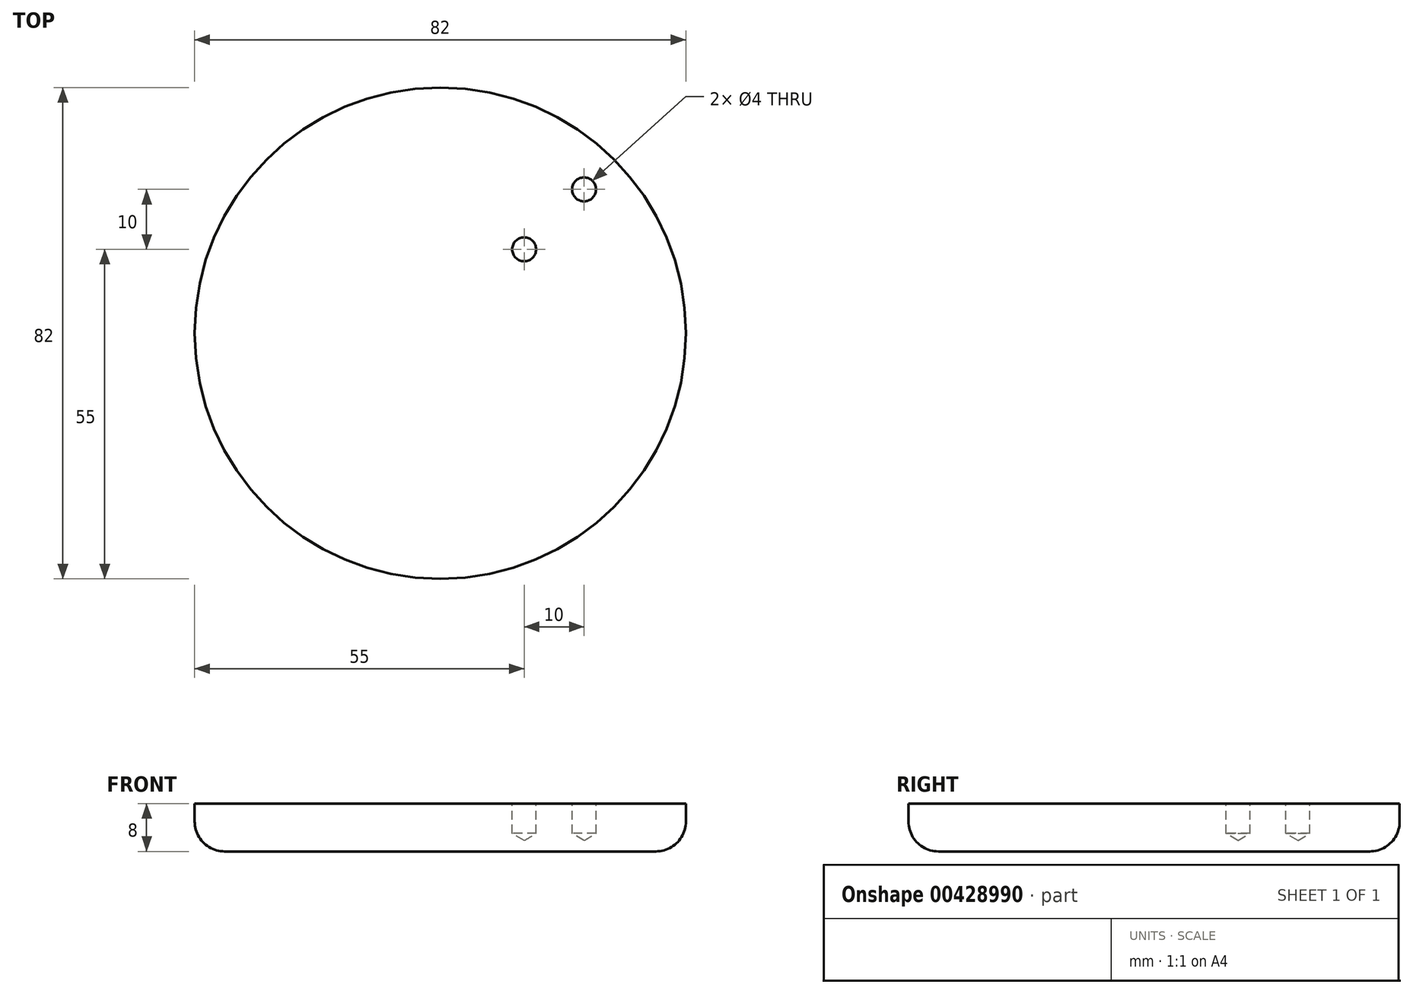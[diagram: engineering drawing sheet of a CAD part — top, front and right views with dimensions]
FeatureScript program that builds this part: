
annotation { "Feature Type Name" : "Feature", "Feature Type Description" : "" }
export const myFeature = defineFeature(function(context is Context, id is Id, definition is map)
    precondition{}
    {
        {
            var Q0;
            Q0=qCreatedBy(makeId("Top.planeOp"),FACE);
            var sketch = newSketch(context, id + "F0", { "sketchPlane" : qUnion([Q0])});
            skCircle(sketch, "E0", {"center": v(0, 0) * mm, "radius": 41 * mm});
            skSolve(sketch);
        }
        {
            var Q0;
            Q0 = qSketchRegion(id + "F0", true);
            extrude(context, id + "F1", {"entities" : qUnion([Q0]), "depth" : 8 * mm});
        }
        {
            var Q0;
            Q0=makeQuery(id+"F1.opExtrude","CAP_FACE",FACE,{"disambiguationData":[OSD([sQuery(id+"F0.wireOp",EDGE,"E0")])],"isStart":true});
            fillet(context, id + "F2", {"entities" : qUnion([Q0]), "radius" : 5 * mm, "tangentPropagation" : true, "allowEdgeOverflow" : false});
        }
        {
            var Q0;
            Q0=makeQuery(id+"F1.opExtrude","CAP_FACE",FACE,{"disambiguationData":[OSD([sQuery(id+"F0.wireOp",EDGE,"E0")])],"isStart":false});
            var sketch = newSketch(context, id + "F3", { "sketchPlane" : qUnion([Q0])});
            skLineSegment(sketch, "E1", {"start": v(0, 0) * mm, "end": v(33.6, 33.6) * mm, "construction": true});
            skCircle(sketch, "E2", {"center": v(14, 14) * mm, "radius": 2 * mm});
            skCircle(sketch, "E3", {"center": v(24, 24) * mm, "radius": 2 * mm});
            skSolve(sketch);
        }
        {
            var Q0;
            Q0=sQuery(id+"F3.wireOp",VERTEX,"E2.center");
            var Q1;
            Q1=sQuery(id+"F3.wireOp",VERTEX,"E3.center");
            var Q2;
            Q2=makeQuery(id+"F1.opExtrude","SWEPT_BODY",BODY,{"disambiguationData":[OSD([sQuery(id+"F0.wireOp",EDGE,"E0")])]});
            hole(context, id + "F4", {"style" : HoleStyle.SIMPLE, "endStyle" : HoleEndStyle.BLIND, "holeDiameter" : 4 * mm, "holeDepth" : 5 * mm, "isTappedThrough" : true, "tappedDepth" : 12 * mm, "tapClearance" : 3, "startFromSketch" : true, "locations" : qUnion([Q0, Q1]), "scope" : qUnion([Q2])});
        }
        {
            var Q0;
            Q0=qCreatedBy(makeId("Front.planeOp"),FACE);
            var sketch = newSketch(context, id + "F5", { "sketchPlane" : qUnion([Q0])});
            skLineSegment(sketch, "E4", {"start": v(0, 0) * mm, "end": v(0, 22.56) * mm, "construction": true});
            skSolve(sketch);
        }
    });
